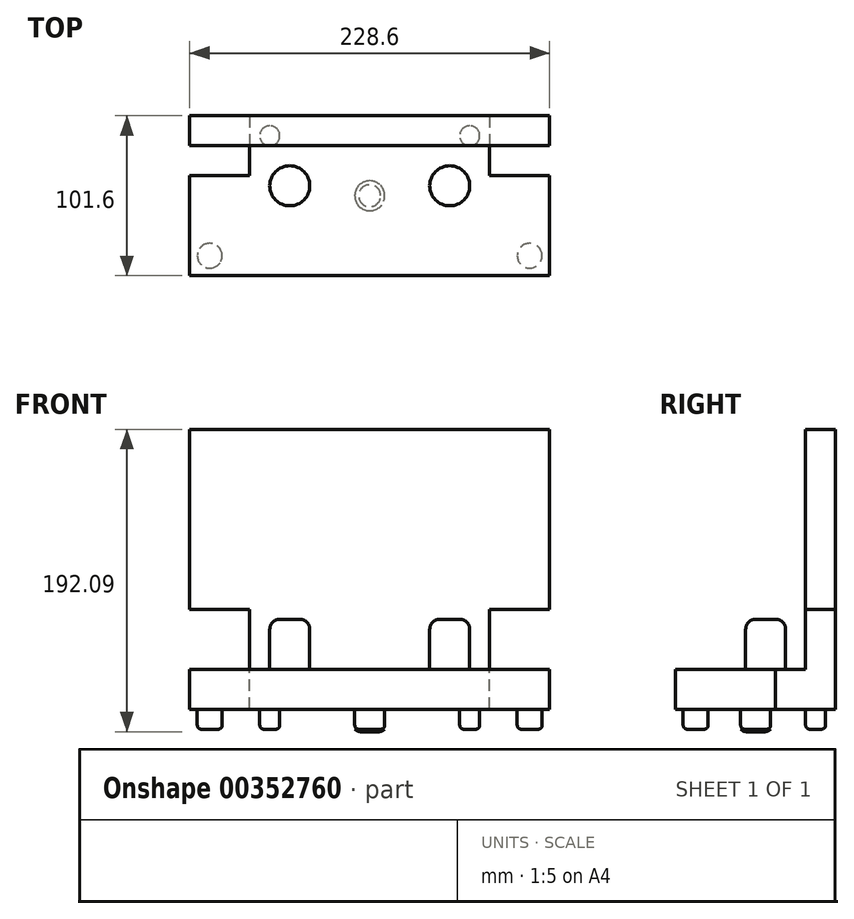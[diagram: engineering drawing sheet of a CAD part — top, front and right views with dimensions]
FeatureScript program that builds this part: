
annotation { "Feature Type Name" : "Feature", "Feature Type Description" : "" }
export const myFeature = defineFeature(function(context is Context, id is Id, definition is map)
    precondition{}
    {
        {
            var Q0;
            Q0=qCreatedBy(makeId("Front.planeOp"),FACE);
            var sketch = newSketch(context, id + "F0", { "sketchPlane" : qUnion([Q0])});
            skLineSegment(sketch, "E0.bottom", {"start": v(0, 0) * mm, "end": v(228.6, 0) * mm});
            skLineSegment(sketch, "E0.top", {"start": v(0, 101.6) * mm, "end": v(228.6, 101.6) * mm});
            skLineSegment(sketch, "E0.left", {"start": v(0, 0) * mm, "end": v(0, 101.6) * mm});
            skLineSegment(sketch, "E0.right", {"start": v(228.6, 0) * mm, "end": v(228.6, 101.6) * mm});
            skSolve(sketch);
        }
        {
            var Q0;
            Q0 = qSketchRegion(id + "F0", true);
            extrude(context, id + "F1", {"entities" : qUnion([Q0]), "oppositeDirection" : true, "depth" : 177.8 * mm});
        }
        {
            var Q0;
            Q0=makeQuery(id+"F1.opExtrude","CAP_FACE",FACE,{"disambiguationData":[OSD([sQuery(id+"F0.wireOp",EDGE,"E0.bottom"),sQuery(id+"F0.wireOp",EDGE,"E0.top"),sQuery(id+"F0.wireOp",EDGE,"E0.left"),sQuery(id+"F0.wireOp",EDGE,"E0.right")])],"isStart":true});
            var sketch = newSketch(context, id + "F2", { "sketchPlane" : qUnion([Q0])});
            skPoint(sketch, "E1", {"position": v(0, 19.05) * mm});
            skLineSegment(sketch, "E2.bottom", {"start": v(0, 19.05) * mm, "end": v(228.6, 19.05) * mm});
            skLineSegment(sketch, "E2.top", {"start": v(0, 101.6) * mm, "end": v(228.6, 101.6) * mm});
            skLineSegment(sketch, "E2.left", {"start": v(0, 19.05) * mm, "end": v(0, 101.6) * mm});
            skLineSegment(sketch, "E2.right", {"start": v(228.6, 19.05) * mm, "end": v(228.6, 101.6) * mm});
            skSolve(sketch);
        }
        {
            var Q0;
            Q0 = qSketchRegion(id + "F2", true);
            extrude(context, id + "F3", {"entities" : qUnion([Q0]), "operationType" : NewBodyOperationType.REMOVE, "oppositeDirection" : true, "depth" : 152.4 * mm});
        }
        {
            var Q0;
            Q0=makeQuery(id+"F3.boolean.opBoolean","COPY",FACE,{"derivedFrom":makeQuery(id+"F3.opExtrude","CAP_FACE",FACE,{"disambiguationData":[OSD([sQuery(id+"F2.wireOp",EDGE,"E2.bottom"),sQuery(id+"F2.wireOp",EDGE,"E2.top"),sQuery(id+"F2.wireOp",EDGE,"E2.left"),sQuery(id+"F2.wireOp",EDGE,"E2.right")])],"isStart":false})});
            var sketch = newSketch(context, id + "F4", { "sketchPlane" : qUnion([Q0])});
            skCircle(sketch, "E3", {"center": v(63.5, 44.45) * mm, "radius": 12.7 * mm});
            skCircle(sketch, "E4", {"center": v(165.1, 44.45) * mm, "radius": 12.7 * mm});
            skSolve(sketch);
        }
        {
            var Q0;
            Q0 = qSketchRegion(id + "F4", true);
            extrude(context, id + "F5", {"entities" : qUnion([Q0]), "operationType" : NewBodyOperationType.ADD, "depth" : 31.75 * mm});
        }
        {
            var Q0;
            Q0=makeQuery(id+"F5.opExtrude","CAP_EDGE",EDGE,{"disambiguationData":[OSD([sQuery(id+"F4.wireOp",EDGE,"E3")])],"isStart":false});
            var Q1;
            Q1=makeQuery(id+"F5.opExtrude","CAP_EDGE",EDGE,{"disambiguationData":[OSD([sQuery(id+"F4.wireOp",EDGE,"E4")])],"isStart":false});
            fillet(context, id + "F6", {"entities" : qUnion([Q0, Q1]), "radius" : 6.35 * mm, "tangentPropagation" : true, "allowEdgeOverflow" : false});
        }
        {
            var Q0;
            Q0=makeQuery(id+"F1.opExtrude","SWEPT_BODY",BODY,{"disambiguationData":[OSD([sQuery(id+"F0.wireOp",EDGE,"E0.bottom"),sQuery(id+"F0.wireOp",EDGE,"E0.top"),sQuery(id+"F0.wireOp",EDGE,"E0.left"),sQuery(id+"F0.wireOp",EDGE,"E0.right")])]});
            var Q1;
            Q1=makeQuery(id+"F1.opExtrude","CAP_EDGE",EDGE,{"disambiguationData":[OSD([sQuery(id+"F0.wireOp",EDGE,"E0.bottom")])],"isStart":true});
            transform(context, id + "F7", {"entities" : qUnion([Q0]), "transformType" : TransformType.ROTATION, "transformAxis" : qUnion([Q1]), "angle" : 90 * degree, "oppositeDirection" : true, "makeCopy" : false});
        }
        {
            var Q0;
            Q0=makeQuery(id+"F1.opExtrude","SWEPT_BODY",BODY,{"disambiguationData":[OSD([sQuery(id+"F0.wireOp",EDGE,"E0.bottom"),sQuery(id+"F0.wireOp",EDGE,"E0.top"),sQuery(id+"F0.wireOp",EDGE,"E0.left"),sQuery(id+"F0.wireOp",EDGE,"E0.right")])]});
            var Q1;
            Q1=makeQuery(id+"F1.opExtrude","CAP_FACE",FACE,{"disambiguationData":[OSD([sQuery(id+"F0.wireOp",EDGE,"E0.bottom"),sQuery(id+"F0.wireOp",EDGE,"E0.top"),sQuery(id+"F0.wireOp",EDGE,"E0.left"),sQuery(id+"F0.wireOp",EDGE,"E0.right")])],"isStart":true});
            transform(context, id + "F8", {"entities" : qUnion([Q0]), "transformType" : TransformType.TRANSLATION_DISTANCE, "transformDirection" : qUnion([Q1]), "distance" : 177.8 * mm, "makeCopy" : false});
        }
        {
            var Q0;
            Q0=makeQuery(id+"F1.opExtrude","SWEPT_BODY",BODY,{"disambiguationData":[OSD([sQuery(id+"F0.wireOp",EDGE,"E0.bottom"),sQuery(id+"F0.wireOp",EDGE,"E0.top"),sQuery(id+"F0.wireOp",EDGE,"E0.left"),sQuery(id+"F0.wireOp",EDGE,"E0.right")])]});
            var Q1;
            Q1=makeQuery(id+"F1.opExtrude","SWEPT_EDGE",EDGE,{"disambiguationData":[OSD([sQuery(id+"F0.wireOp",EDGE,"E0.bottom"),sQuery(id+"F0.wireOp",EDGE,"E0.left")])]});
            transform(context, id + "F9", {"entities" : qUnion([Q0]), "transformType" : TransformType.ROTATION, "transformAxis" : qUnion([Q1]), "angle" : 180 * degree, "makeCopy" : false});
        }
        {
            var Q0;
            Q0=makeQuery(id+"F1.opExtrude","SWEPT_BODY",BODY,{"disambiguationData":[OSD([sQuery(id+"F0.wireOp",EDGE,"E0.bottom"),sQuery(id+"F0.wireOp",EDGE,"E0.top"),sQuery(id+"F0.wireOp",EDGE,"E0.left"),sQuery(id+"F0.wireOp",EDGE,"E0.right")])]});
            var Q1;
            Q1=makeQuery(id+"F1.opExtrude","SWEPT_FACE",FACE,{"disambiguationData":[OSD([sQuery(id+"F0.wireOp",EDGE,"E0.left")])]});
            transform(context, id + "F10", {"entities" : qUnion([Q0]), "transformType" : TransformType.TRANSLATION_DISTANCE, "transformDirection" : qUnion([Q1]), "distance" : 228.6 * mm, "makeCopy" : false});
        }
        {
            var Q0;
            Q0=makeQuery(id+"F3.boolean.opBoolean","COPY",FACE,{"derivedFrom":makeQuery(id+"F3.opExtrude","SWEPT_FACE",FACE,{"disambiguationData":[OSD([sQuery(id+"F2.wireOp",EDGE,"E2.bottom")])]})});
            var sketch = newSketch(context, id + "F11", { "sketchPlane" : qUnion([Q0])});
            skPoint(sketch, "E5", {"position": v(38.1, 25.4) * mm});
            skPoint(sketch, "E6", {"position": v(190.5, 25.4) * mm});
            skLineSegment(sketch, "E7.bottom", {"start": v(38.1, 25.4) * mm, "end": v(0, 25.4) * mm});
            skLineSegment(sketch, "E7.top", {"start": v(38.1, 63.5) * mm, "end": v(0, 63.5) * mm});
            skLineSegment(sketch, "E7.left", {"start": v(38.1, 25.4) * mm, "end": v(38.1, 63.5) * mm});
            skLineSegment(sketch, "E7.right", {"start": v(0, 25.4) * mm, "end": v(0, 63.5) * mm});
            skLineSegment(sketch, "E8.bottom", {"start": v(190.5, 25.4) * mm, "end": v(228.6, 25.4) * mm});
            skLineSegment(sketch, "E8.top", {"start": v(190.5, 63.5) * mm, "end": v(228.6, 63.5) * mm});
            skLineSegment(sketch, "E8.left", {"start": v(190.5, 25.4) * mm, "end": v(190.5, 63.5) * mm});
            skLineSegment(sketch, "E8.right", {"start": v(228.6, 25.4) * mm, "end": v(228.6, 63.5) * mm});
            skSolve(sketch);
        }
        {
            var Q0;
            Q0 = qSketchRegion(id + "F11", true);
            extrude(context, id + "F12", {"entities" : qUnion([Q0]), "operationType" : NewBodyOperationType.REMOVE, "oppositeDirection" : true, "depth" : 25.4 * mm});
        }
        {
            var Q0;
            Q0=makeQuery(id+"F12.boolean.opBoolean","MERGE",FACE,{"derivedFrom":[makeQuery(id+"F3.boolean.opBoolean","COPY",FACE,{"derivedFrom":makeQuery(id+"F3.opExtrude","CAP_FACE",FACE,{"disambiguationData":[OSD([sQuery(id+"F2.wireOp",EDGE,"E2.bottom"),sQuery(id+"F2.wireOp",EDGE,"E2.top"),sQuery(id+"F2.wireOp",EDGE,"E2.left"),sQuery(id+"F2.wireOp",EDGE,"E2.right")])],"isStart":false})}),makeQuery(id+"F12.opExtrude","SWEPT_FACE",FACE,{"disambiguationData":[OSD([sQuery(id+"F11.wireOp",EDGE,"E7.bottom")])]}),makeQuery(id+"F12.opExtrude","SWEPT_FACE",FACE,{"disambiguationData":[OSD([sQuery(id+"F11.wireOp",EDGE,"E8.bottom")])]})]});
            var sketch = newSketch(context, id + "F13", { "sketchPlane" : qUnion([Q0])});
            skLineSegment(sketch, "E9.bottom", {"start": v(0, 0) * mm, "end": v(38.1, 0) * mm});
            skLineSegment(sketch, "E9.top", {"start": v(0, -38.1) * mm, "end": v(38.1, -38.1) * mm});
            skLineSegment(sketch, "E9.left", {"start": v(0, 0) * mm, "end": v(0, -38.1) * mm});
            skLineSegment(sketch, "E9.right", {"start": v(38.1, 0) * mm, "end": v(38.1, -38.1) * mm});
            skLineSegment(sketch, "E10.bottom", {"start": v(228.6, 0) * mm, "end": v(190.5, 0) * mm});
            skLineSegment(sketch, "E10.top", {"start": v(228.6, -38.1) * mm, "end": v(190.5, -38.1) * mm});
            skLineSegment(sketch, "E10.left", {"start": v(228.6, 0) * mm, "end": v(228.6, -38.1) * mm});
            skLineSegment(sketch, "E10.right", {"start": v(190.5, 0) * mm, "end": v(190.5, -38.1) * mm});
            skSolve(sketch);
        }
        {
            var Q0;
            Q0 = qSketchRegion(id + "F13", true);
            extrude(context, id + "F14", {"entities" : qUnion([Q0]), "operationType" : NewBodyOperationType.REMOVE, "oppositeDirection" : true, "depth" : 25.4 * mm});
        }
        {
            var Q0;
            Q0=makeQuery(id+"F1.opExtrude","CAP_FACE",FACE,{"disambiguationData":[OSD([sQuery(id+"F0.wireOp",EDGE,"E0.bottom"),sQuery(id+"F0.wireOp",EDGE,"E0.top"),sQuery(id+"F0.wireOp",EDGE,"E0.left"),sQuery(id+"F0.wireOp",EDGE,"E0.right")])],"isStart":false});
            var sketch = newSketch(context, id + "F15", { "sketchPlane" : qUnion([Q0])});
            skCircle(sketch, "E11", {"center": v(215.9, 88.9) * mm, "radius": 7.94 * mm});
            skCircle(sketch, "E12", {"center": v(12.7, 88.9) * mm, "radius": 7.94 * mm});
            skCircle(sketch, "E13", {"center": v(50.8, 12.7) * mm, "radius": 6.35 * mm});
            skCircle(sketch, "E14", {"center": v(177.8, 12.7) * mm, "radius": 6.35 * mm});
            skCircle(sketch, "E15", {"center": v(114.3, 50.8) * mm, "radius": 9.53 * mm});
            skSolve(sketch);
        }
        {
            var Q0;
            Q0 = qSketchRegion(id + "F15", true);
            extrude(context, id + "F16", {"entities" : qUnion([Q0]), "operationType" : NewBodyOperationType.ADD, "depth" : 12.7 * mm});
        }
        {
            var Q0;
            Q0=makeQuery(id+"F16.opExtrude","CAP_EDGE",EDGE,{"disambiguationData":[OSD([sQuery(id+"F15.wireOp",EDGE,"E12")])],"isStart":false});
            var Q1;
            Q1=makeQuery(id+"F16.opExtrude","CAP_EDGE",EDGE,{"disambiguationData":[OSD([sQuery(id+"F15.wireOp",EDGE,"E13")])],"isStart":false});
            var Q2;
            Q2=makeQuery(id+"F16.opExtrude","CAP_EDGE",EDGE,{"disambiguationData":[OSD([sQuery(id+"F15.wireOp",EDGE,"E14")])],"isStart":false});
            var Q3;
            Q3=makeQuery(id+"F16.opExtrude","CAP_EDGE",EDGE,{"disambiguationData":[OSD([sQuery(id+"F15.wireOp",EDGE,"E11")])],"isStart":false});
            var Q4;
            Q4=makeQuery(id+"F16.opExtrude","CAP_EDGE",EDGE,{"disambiguationData":[OSD([sQuery(id+"F15.wireOp",EDGE,"E15")])],"isStart":false});
            fillet(context, id + "F17", {"entities" : qUnion([Q0, Q1, Q2, Q3, Q4]), "radius" : 2.54 * mm, "tangentPropagation" : true, "allowEdgeOverflow" : false});
        }
        {
            var Q0;
            Q0=makeQuery(id+"F16.opExtrude","CAP_FACE",FACE,{"disambiguationData":[OSD([sQuery(id+"F15.wireOp",EDGE,"E15")])],"isStart":false});
            var sketch = newSketch(context, id + "F18", { "sketchPlane" : qUnion([Q0])});
            skCircle(sketch, "E16", {"center": v(114.3, 50.8) * mm, "radius": 9.53 * mm});
            skSolve(sketch);
        }
        {
            var Q0;
            Q0 = qSketchRegion(id + "F18", true);
            extrude(context, id + "F19", {"entities" : qUnion([Q0]), "operationType" : NewBodyOperationType.ADD, "depth" : 1.59 * mm});
        }
        {
            var Q0;
            Q0=makeQuery(id+"F19.opExtrude","CAP_EDGE",EDGE,{"disambiguationData":[OSD([sQuery(id+"F18.wireOp",EDGE,"E16")])],"isStart":false});
            fillet(context, id + "F20", {"entities" : qUnion([Q0]), "radius" : 5.08 * mm, "tangentPropagation" : true, "allowEdgeOverflow" : false});
        }
    });
